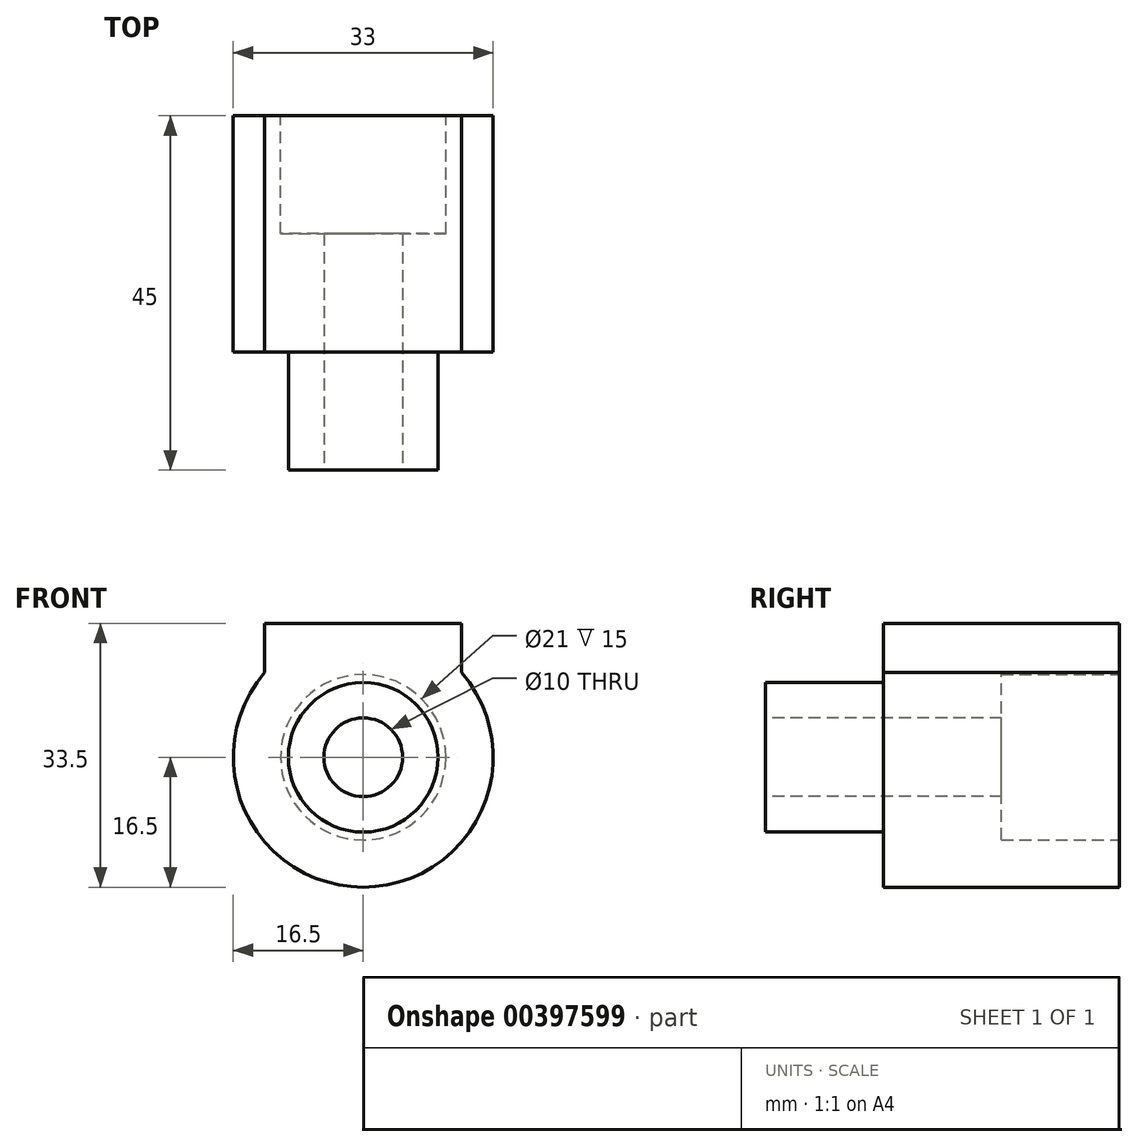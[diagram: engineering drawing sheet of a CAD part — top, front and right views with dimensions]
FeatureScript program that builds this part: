
annotation { "Feature Type Name" : "Feature", "Feature Type Description" : "" }
export const myFeature = defineFeature(function(context is Context, id is Id, definition is map)
    precondition{}
    {
        {
            var Q0;
            Q0=qCreatedBy(makeId("Front.planeOp"),FACE);
            var sketch = newSketch(context, id + "F0", { "sketchPlane" : qUnion([Q0])});
            skCircle(sketch, "E0", {"center": v(0, 0) * mm, "radius": 16.5 * mm});
            skSolve(sketch);
        }
        {
            var Q0;
            Q0=qSketchRegion(id+"F0",true);
            extrude(context, id + "F1", {"entities" : qUnion([Q0]), "depth" : 30 * mm});
        }
        {
            var Q0;
            Q0=qCreatedBy(makeId("Top.planeOp"),FACE);
            var sketch = newSketch(context, id + "F2", { "sketchPlane" : qUnion([Q0])});
            skLineSegment(sketch, "E1", {"start": v(0, 0) * mm, "end": v(0, -30) * mm});
            skLineSegment(sketch, "E2.bottom", {"start": v(-12.5, 0) * mm, "end": v(12.5, 0) * mm});
            skLineSegment(sketch, "E2.top", {"start": v(-12.5, -30) * mm, "end": v(12.5, -30) * mm});
            skLineSegment(sketch, "E2.left", {"start": v(-12.5, 0) * mm, "end": v(-12.5, -30) * mm});
            skLineSegment(sketch, "E2.right", {"start": v(12.5, 0) * mm, "end": v(12.5, -30) * mm});
            skPoint(sketch, "E2.middle", {"position": v(0, -15) * mm});
            skSolve(sketch);
        }
        {
            var Q0;
            Q0=qSketchRegion(id+"F2",true);
            extrude(context, id + "F3", {"entities" : qUnion([Q0]), "operationType" : NewBodyOperationType.ADD, "depth" : 17 * mm});
        }
        {
            var Q0;
            Q0=makeQuery(id+"F3.boolean.opBoolean","MERGE",FACE,{"derivedFrom":[makeQuery(id+"F1.opExtrude","CAP_FACE",FACE,{"disambiguationData":[OSD([sQuery(id+"F0.wireOp",EDGE,"E0")])],"isStart":false}),makeQuery(id+"F3.opExtrude","SWEPT_FACE",FACE,{"disambiguationData":[OSD([sQuery(id+"F2.wireOp",EDGE,"E2.top")])]})]});
            var sketch = newSketch(context, id + "F4", { "sketchPlane" : qUnion([Q0])});
            skCircle(sketch, "E3", {"center": v(0, 0) * mm, "radius": 9.5 * mm});
            skSolve(sketch);
        }
        {
            var Q0;
            Q0=qSketchRegion(id+"F4",true);
            extrude(context, id + "F5", {"entities" : qUnion([Q0]), "operationType" : NewBodyOperationType.ADD, "depth" : 15 * mm});
        }
        {
            var Q0;
            Q0=qCreatedBy(makeId("Front.planeOp"),FACE);
            var sketch = newSketch(context, id + "F6", { "sketchPlane" : qUnion([Q0])});
            skCircle(sketch, "E4", {"center": v(0, 0) * mm, "radius": 10.5 * mm});
            skSolve(sketch);
        }
        {
            var Q0;
            Q0=makeQuery(id+"F6.imprint","IMPRINT",FACE,{"disambiguationData":[TD([[makeQuery(id+"F6.imprint","IMPRINT",EDGE,{"derivedFrom":sQuery(id+"F6.wireOp",EDGE,"E4")}),1.0]])]});
            extrude(context, id + "F7", {"entities" : qUnion([Q0]), "operationType" : NewBodyOperationType.REMOVE, "depth" : 15 * mm});
        }
        {
            var Q0;
            Q0=makeQuery(id+"F5.opExtrude","CAP_FACE",FACE,{"disambiguationData":[OSD([sQuery(id+"F4.wireOp",EDGE,"E3")])],"isStart":false});
            var sketch = newSketch(context, id + "F8", { "sketchPlane" : qUnion([Q0])});
            skCircle(sketch, "E5", {"center": v(0, 0) * mm, "radius": 5 * mm});
            skSolve(sketch);
        }
        {
            var Q0;
            Q0=qSketchRegion(id+"F8",true);
            extrude(context, id + "F9", {"entities" : qUnion([Q0]), "operationType" : NewBodyOperationType.REMOVE, "oppositeDirection" : true, "depth" : 77 * mm});
        }
    });
